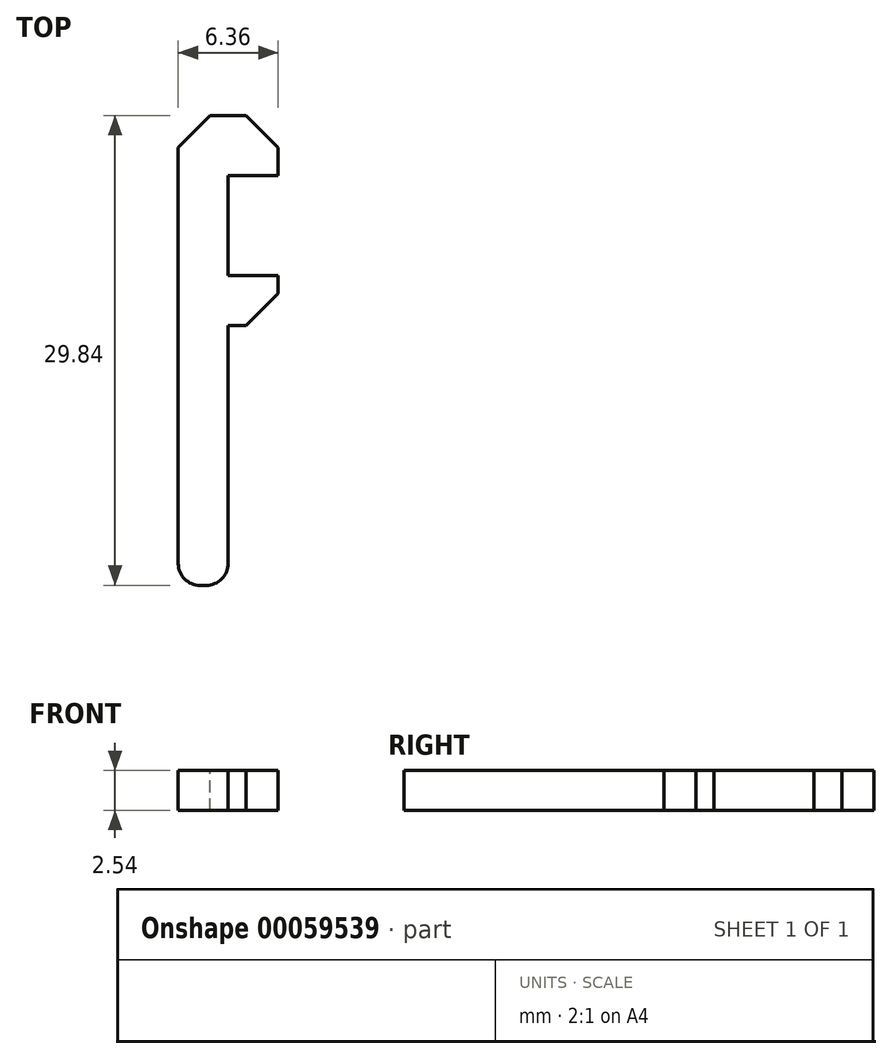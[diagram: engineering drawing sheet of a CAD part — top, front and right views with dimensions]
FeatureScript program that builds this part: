
annotation { "Feature Type Name" : "Feature", "Feature Type Description" : "" }
export const myFeature = defineFeature(function(context is Context, id is Id, definition is map)
    precondition{}
    {
        {
            var Q0;
            Q0=qCreatedBy(makeId("Top.planeOp"),FACE);
            var sketch = newSketch(context, id + "F0", { "sketchPlane" : qUnion([Q0])});
            skLineSegment(sketch, "E0.rect.top", {"start": v(3.18, 14.92) * mm, "end": v(-3.18, 14.92) * mm});
            skLineSegment(sketch, "E0.rect.right", {"start": v(-3.18, -14.92) * mm, "end": v(-3.18, 14.92) * mm});
            skPoint(sketch, "E0.rect.middle", {"position": v(0, 0) * mm});
            skLineSegment(sketch, "E1", {"start": v(0, 11.11) * mm, "end": v(3.17, 11.11) * mm});
            skLineSegment(sketch, "E2", {"start": v(3.17, 14.92) * mm, "end": v(3.17, 11.11) * mm});
            skLineSegment(sketch, "E3", {"start": v(-3.18, -14.92) * mm, "end": v(0, -14.92) * mm});
            skLineSegment(sketch, "E4", {"start": v(3.17, 1.59) * mm, "end": v(3.17, 4.76) * mm});
            skLineSegment(sketch, "E5", {"start": v(0, -14.92) * mm, "end": v(0, 1.59) * mm});
            skLineSegment(sketch, "E6", {"start": v(0, 1.59) * mm, "end": v(3.17, 1.59) * mm});
            skLineSegment(sketch, "E7", {"start": v(0, 4.76) * mm, "end": v(3.17, 4.76) * mm});
            skLineSegment(sketch, "E8", {"start": v(0, 11.11) * mm, "end": v(0, 4.76) * mm});
            skSolve(sketch);
        }
        {
            var Q0;
            Q0=makeQuery(id+"F0.imprint","IMPRINT",FACE,{"disambiguationData":[TD([[makeQuery(id+"F0.imprint","IMPRINT",EDGE,{"derivedFrom":sQuery(id+"F0.wireOp",EDGE,"E0.rect.top")}),1.0]])]});
            extrude(context, id + "F1", {"entities" : qUnion([Q0]), "depth" : 2.54 * mm});
        }
        {
            var Q0;
            Q0=makeQuery(id+"F1.opExtrude","SWEPT_EDGE",EDGE,{"disambiguationData":[OSD([sQuery(id+"F0.wireOp",EDGE,"E4"),sQuery(id+"F0.wireOp",EDGE,"E6")])]});
            var Q1;
            Q1=makeQuery(id+"F1.opExtrude","SWEPT_EDGE",EDGE,{"disambiguationData":[OSD([sQuery(id+"F0.wireOp",EDGE,"E0.rect.top"),sQuery(id+"F0.wireOp",EDGE,"E2")])]});
            var Q2;
            Q2=makeQuery(id+"F1.opExtrude","SWEPT_EDGE",EDGE,{"disambiguationData":[OSD([sQuery(id+"F0.wireOp",EDGE,"E0.rect.top"),sQuery(id+"F0.wireOp",EDGE,"E0.rect.right")])]});
            chamfer(context, id + "F2", {"entities" : qUnion([Q0, Q1, Q2]), "width" : 2.03 * mm, "tangentPropagation" : true});
        }
        {
            var Q0;
            Q0=makeQuery(id+"F1.opExtrude","SWEPT_EDGE",EDGE,{"disambiguationData":[OSD([sQuery(id+"F0.wireOp",EDGE,"E3"),sQuery(id+"F0.wireOp",EDGE,"E5")])]});
            fillet(context, id + "F3", {"entities" : qUnion([Q0]), "radius" : 1.4 * mm, "tangentPropagation" : true, "allowEdgeOverflow" : false});
        }
        {
            var Q0;
            Q0=makeQuery(id+"F1.opExtrude","SWEPT_EDGE",EDGE,{"disambiguationData":[OSD([sQuery(id+"F0.wireOp",EDGE,"E0.rect.right"),sQuery(id+"F0.wireOp",EDGE,"E3")])]});
            fillet(context, id + "F4", {"entities" : qUnion([Q0]), "radius" : 1.39 * mm, "tangentPropagation" : true, "allowEdgeOverflow" : false});
        }
    });
